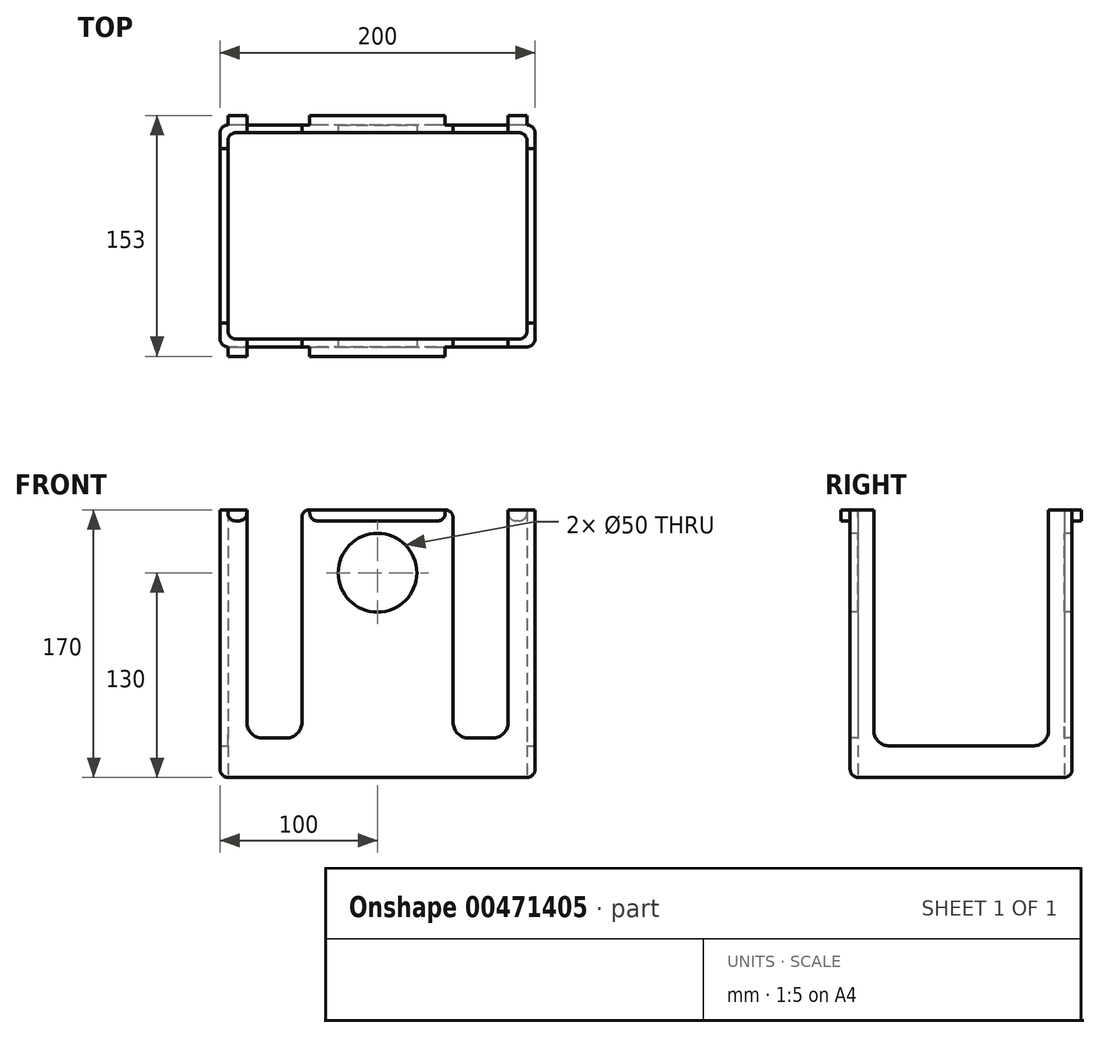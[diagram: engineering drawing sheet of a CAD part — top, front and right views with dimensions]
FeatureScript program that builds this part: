
annotation { "Feature Type Name" : "Feature", "Feature Type Description" : "" }
export const myFeature = defineFeature(function(context is Context, id is Id, definition is map)
    precondition{}
    {
        {
            var Q0;
            Q0=qCreatedBy(makeId("Top.planeOp"),FACE);
            var sketch = newSketch(context, id + "F0", { "sketchPlane" : qUnion([Q0])});
            skLineSegment(sketch, "E0.bottom", {"start": v(95, 70.5) * mm, "end": v(-95, 70.5) * mm});
            skLineSegment(sketch, "E0.top", {"start": v(95, -70.5) * mm, "end": v(-95, -70.5) * mm});
            skLineSegment(sketch, "E0.left", {"start": v(100, 65.5) * mm, "end": v(100, -65.5) * mm});
            skLineSegment(sketch, "E0.right", {"start": v(-100, 65.5) * mm, "end": v(-100, -65.5) * mm});
            skPoint(sketch, "E0.middle", {"position": v(0, 0) * mm});
            skPoint(sketch, "E1.visualSharp", {"position": v(-100, 70.5) * mm});
            skArc(sketch, "E1.filletArc", {"start": v(-95, 70.5) * mm, "mid": v(-98.54, 69.04) * mm, "end": v(-100, 65.5) * mm});
            skPoint(sketch, "E2.visualSharp", {"position": v(100, 70.5) * mm});
            skArc(sketch, "E2.filletArc", {"start": v(100, 65.5) * mm, "mid": v(98.54, 69.04) * mm, "end": v(95, 70.5) * mm});
            skPoint(sketch, "E3.visualSharp", {"position": v(100, -70.5) * mm});
            skArc(sketch, "E3.filletArc", {"start": v(95, -70.5) * mm, "mid": v(98.54, -69.04) * mm, "end": v(100, -65.5) * mm});
            skPoint(sketch, "E4.visualSharp", {"position": v(-100, -70.5) * mm});
            skArc(sketch, "E4.filletArc", {"start": v(-100, -65.5) * mm, "mid": v(-98.54, -69.04) * mm, "end": v(-95, -70.5) * mm});
            skLineSegment(sketch, "E5.bottom", {"start": v(90, 65.5) * mm, "end": v(-90, 65.5) * mm});
            skLineSegment(sketch, "E5.top", {"start": v(90, -65.5) * mm, "end": v(-90, -65.5) * mm});
            skLineSegment(sketch, "E5.left", {"start": v(95, 60.5) * mm, "end": v(95, -60.5) * mm});
            skLineSegment(sketch, "E5.right", {"start": v(-95, 60.5) * mm, "end": v(-95, -60.5) * mm});
            skArc(sketch, "E6.filletArc", {"start": v(-90, 65.5) * mm, "mid": v(-93.54, 64.04) * mm, "end": v(-95, 60.5) * mm});
            skArc(sketch, "E7.filletArc", {"start": v(95, 60.5) * mm, "mid": v(93.54, 64.04) * mm, "end": v(90, 65.5) * mm});
            skArc(sketch, "E8.filletArc", {"start": v(90, -65.5) * mm, "mid": v(93.54, -64.04) * mm, "end": v(95, -60.5) * mm});
            skArc(sketch, "E9.filletArc", {"start": v(-95, -60.5) * mm, "mid": v(-93.54, -64.04) * mm, "end": v(-90, -65.5) * mm});
            skSolve(sketch);
        }
        {
            var Q0;
            Q0 = qSketchRegion(id + "F0", true);
            extrude(context, id + "F1", {"entities" : qUnion([Q0]), "depth" : 170 * mm});
        }
        {
            var Q0;
            Q0=makeQuery(id+"F1.opExtrude","SWEPT_FACE",FACE,{"disambiguationData":[OSD([sQuery(id+"F0.wireOp",EDGE,"E0.top")])]});
            var sketch = newSketch(context, id + "F2", { "sketchPlane" : qUnion([Q0])});
            skCircle(sketch, "E10", {"center": v(0, 130) * mm, "radius": 25 * mm});
            skLineSegment(sketch, "E11.bottom", {"start": v(-83, 170) * mm, "end": v(-48, 170) * mm});
            skLineSegment(sketch, "E11.top", {"start": v(-73, 25) * mm, "end": v(-58, 25) * mm});
            skLineSegment(sketch, "E11.left", {"start": v(-83, 170) * mm, "end": v(-83, 35) * mm});
            skLineSegment(sketch, "E11.right", {"start": v(-48, 170) * mm, "end": v(-48, 35) * mm});
            skLineSegment(sketch, "E12.bottom", {"start": v(48, 170) * mm, "end": v(83, 170) * mm});
            skLineSegment(sketch, "E12.top", {"start": v(58, 25) * mm, "end": v(73, 25) * mm});
            skLineSegment(sketch, "E12.left", {"start": v(48, 170) * mm, "end": v(48, 35) * mm});
            skLineSegment(sketch, "E12.right", {"start": v(83, 170) * mm, "end": v(83, 35) * mm});
            skPoint(sketch, "E13.visualSharp", {"position": v(-83, 25) * mm});
            skArc(sketch, "E13.filletArc", {"start": v(-83, 35) * mm, "mid": v(-80.07, 27.93) * mm, "end": v(-73, 25) * mm});
            skPoint(sketch, "E14.visualSharp", {"position": v(-48, 25) * mm});
            skArc(sketch, "E14.filletArc", {"start": v(-58, 25) * mm, "mid": v(-50.93, 27.93) * mm, "end": v(-48, 35) * mm});
            skPoint(sketch, "E15.visualSharp", {"position": v(48, 25) * mm});
            skArc(sketch, "E15.filletArc", {"start": v(48, 35) * mm, "mid": v(50.93, 27.93) * mm, "end": v(58, 25) * mm});
            skPoint(sketch, "E16.visualSharp", {"position": v(83, 25) * mm});
            skArc(sketch, "E16.filletArc", {"start": v(73, 25) * mm, "mid": v(80.07, 27.93) * mm, "end": v(83, 35) * mm});
            skSolve(sketch);
        }
        {
            var Q0;
            Q0=makeQuery(id+"F2.imprint","IMPRINT",FACE,{"disambiguationData":[TD([[makeQuery(id+"F2.imprint","IMPRINT",EDGE,{"derivedFrom":sQuery(id+"F2.wireOp",EDGE,"E10")}),1.0]])]});
            var Q1;
            Q1=makeQuery(id+"F2.imprint","IMPRINT",FACE,{"disambiguationData":[TD([[makeQuery(id+"F2.imprint","IMPRINT",EDGE,{"derivedFrom":sQuery(id+"F2.wireOp",EDGE,"E11.bottom")}),1.0]])]});
            var Q2;
            Q2=makeQuery(id+"F2.imprint","IMPRINT",FACE,{"disambiguationData":[TD([[makeQuery(id+"F2.imprint","IMPRINT",EDGE,{"derivedFrom":sQuery(id+"F2.wireOp",EDGE,"E12.bottom")}),1.0]])]});
            extrude(context, id + "F3", {"entities" : qUnion([Q0, Q1, Q2]), "operationType" : NewBodyOperationType.REMOVE, "oppositeDirection" : true, "depth" : 250 * mm});
        }
        {
            var Q0;
            Q0=makeQuery(id+"F1.opExtrude","SWEPT_FACE",FACE,{"disambiguationData":[OSD([sQuery(id+"F0.wireOp",EDGE,"E0.left")])]});
            var sketch = newSketch(context, id + "F4", { "sketchPlane" : qUnion([Q0])});
            skLineSegment(sketch, "E17.bottom", {"start": v(-55.5, 170) * mm, "end": v(55.5, 170) * mm});
            skLineSegment(sketch, "E17.top", {"start": v(-45.5, 20) * mm, "end": v(45.5, 20) * mm});
            skLineSegment(sketch, "E17.left", {"start": v(-55.5, 170) * mm, "end": v(-55.5, 30) * mm});
            skLineSegment(sketch, "E17.right", {"start": v(55.5, 170) * mm, "end": v(55.5, 30) * mm});
            skPoint(sketch, "E18.visualSharp", {"position": v(-55.5, 170) * mm});
            skLineSegment(sketch, "E18.filletArc", {"start": v(-55.5, 170) * mm, "end": v(-55.5, 170) * mm});
            skPoint(sketch, "E19.visualSharp", {"position": v(55.5, 170) * mm});
            skLineSegment(sketch, "E19.filletArc", {"start": v(55.5, 170) * mm, "end": v(55.5, 170) * mm});
            skPoint(sketch, "E20.visualSharp", {"position": v(-55.5, 20) * mm});
            skArc(sketch, "E20.filletArc", {"start": v(-55.5, 30) * mm, "mid": v(-52.57, 22.93) * mm, "end": v(-45.5, 20) * mm});
            skPoint(sketch, "E21.visualSharp", {"position": v(55.5, 20) * mm});
            skArc(sketch, "E21.filletArc", {"start": v(45.5, 20) * mm, "mid": v(52.57, 22.93) * mm, "end": v(55.5, 30) * mm});
            skSolve(sketch);
        }
        {
            var Q0;
            Q0=makeQuery(id+"F4.imprint","IMPRINT",FACE,{"disambiguationData":[TD([[makeQuery(id+"F4.imprint","IMPRINT",EDGE,{"derivedFrom":sQuery(id+"F4.wireOp",EDGE,"E17.bottom")}),1.0]])]});
            extrude(context, id + "F5", {"entities" : qUnion([Q0]), "operationType" : NewBodyOperationType.REMOVE, "oppositeDirection" : true, "depth" : 210 * mm});
        }
        {
            var Q0;
            {var subQ1=sQuery(id+"F0.wireOp",EDGE,"E0.top");var subQ2=sQuery(id+"F2.wireOp",EDGE,"E11.right");Q0=makeQuery(id+"F3.boolean.opBoolean","COPY",EDGE,{"disambiguationData":[TD([makeQuery(id+"F1.opExtrude","SWEPT_FACE",FACE,{"disambiguationData":[OSD([subQ1])]})])],"derivedFrom":makeQuery(id+"F3.opExtrude","SWEPT_EDGE",EDGE,{"disambiguationData":[OSD([subQ1,sQuery(id+"F2.wireOp",EDGE,"E11.bottom"),subQ2])]})});}
            var Q1;
            {var subQ1=sQuery(id+"F0.wireOp",EDGE,"E0.top");var subQ2=sQuery(id+"F2.wireOp",EDGE,"E12.left");Q1=makeQuery(id+"F3.boolean.opBoolean","COPY",EDGE,{"disambiguationData":[TD([makeQuery(id+"F1.opExtrude","SWEPT_FACE",FACE,{"disambiguationData":[OSD([subQ1])]})])],"derivedFrom":makeQuery(id+"F3.opExtrude","SWEPT_EDGE",EDGE,{"disambiguationData":[OSD([subQ1,sQuery(id+"F2.wireOp",EDGE,"E12.bottom"),subQ2])]})});}
            var Q2;
            {var subQ0=sQuery(id+"F0.wireOp",EDGE,"E0.bottom");var subQ2=sQuery(id+"F0.wireOp",EDGE,"E0.top");var subQ3=sQuery(id+"F2.wireOp",EDGE,"E12.left");Q2=makeQuery(id+"F3.boolean.opBoolean","COPY",EDGE,{"disambiguationData":[TD([makeQuery(id+"F1.opExtrude","SWEPT_FACE",FACE,{"disambiguationData":[OSD([subQ0])]})])],"derivedFrom":makeQuery(id+"F3.opExtrude","SWEPT_EDGE",EDGE,{"disambiguationData":[OSD([subQ2,sQuery(id+"F2.wireOp",EDGE,"E12.bottom"),subQ3])]})});}
            var Q3;
            {var subQ0=sQuery(id+"F0.wireOp",EDGE,"E0.bottom");var subQ2=sQuery(id+"F0.wireOp",EDGE,"E0.top");var subQ3=sQuery(id+"F2.wireOp",EDGE,"E11.right");Q3=makeQuery(id+"F3.boolean.opBoolean","COPY",EDGE,{"disambiguationData":[TD([makeQuery(id+"F1.opExtrude","SWEPT_FACE",FACE,{"disambiguationData":[OSD([subQ0])]})])],"derivedFrom":makeQuery(id+"F3.opExtrude","SWEPT_EDGE",EDGE,{"disambiguationData":[OSD([subQ2,sQuery(id+"F2.wireOp",EDGE,"E11.bottom"),subQ3])]})});}
            fillet(context, id + "F6", {"entities" : qUnion([Q0, Q1, Q2, Q3]), "radius" : 5 * mm, "tangentPropagation" : true, "allowEdgeOverflow" : false});
        }
        {
            var Q0;
            Q0=makeQuery(id+"F1.opExtrude","SWEPT_FACE",FACE,{"disambiguationData":[OSD([sQuery(id+"F0.wireOp",EDGE,"E0.top")])]});
            var sketch = newSketch(context, id + "F7", { "sketchPlane" : qUnion([Q0])});
            skLineSegment(sketch, "E22.bottom", {"start": v(-43, 170) * mm, "end": v(43, 170) * mm});
            skLineSegment(sketch, "E22.top", {"start": v(-38.3, 163) * mm, "end": v(38.3, 163) * mm});
            skLineSegment(sketch, "E22.left", {"start": v(-43, 170) * mm, "end": v(-43, 167.7) * mm});
            skLineSegment(sketch, "E22.right", {"start": v(43, 170) * mm, "end": v(43, 167.7) * mm});
            skPoint(sketch, "E23.visualSharp", {"position": v(-43, 163) * mm});
            skArc(sketch, "E23.filletArc", {"start": v(-43, 167.7) * mm, "mid": v(-41.62, 164.38) * mm, "end": v(-38.3, 163) * mm});
            skPoint(sketch, "E24.visualSharp", {"position": v(43, 163) * mm});
            skArc(sketch, "E24.filletArc", {"start": v(38.3, 163) * mm, "mid": v(41.62, 164.38) * mm, "end": v(43, 167.7) * mm});
            skLineSegment(sketch, "E25.bottom", {"start": v(-95, 170) * mm, "end": v(-83, 170) * mm});
            skLineSegment(sketch, "E25.top", {"start": v(-90.3, 163) * mm, "end": v(-88, 163) * mm});
            skLineSegment(sketch, "E25.left", {"start": v(-95, 170) * mm, "end": v(-95, 167.7) * mm});
            skLineSegment(sketch, "E25.right", {"start": v(-83, 170) * mm, "end": v(-83, 168) * mm});
            skPoint(sketch, "E26.visualSharp", {"position": v(-95, 163) * mm});
            skArc(sketch, "E26.filletArc", {"start": v(-95, 167.7) * mm, "mid": v(-93.62, 164.38) * mm, "end": v(-90.3, 163) * mm});
            skPoint(sketch, "E27.visualSharp", {"position": v(-83, 163) * mm});
            skArc(sketch, "E27.filletArc", {"start": v(-88, 163) * mm, "mid": v(-84.46, 164.46) * mm, "end": v(-83, 168) * mm});
            skSolve(sketch);
        }
        {
            var Q0;
            Q0=makeQuery(id+"F7.imprint","IMPRINT",FACE,{"disambiguationData":[TD([[makeQuery(id+"F7.imprint","IMPRINT",EDGE,{"derivedFrom":sQuery(id+"F7.wireOp",EDGE,"E25.bottom")}),1.0]])]});
            var Q1;
            Q1=makeQuery(id+"F7.imprint","IMPRINT",FACE,{"disambiguationData":[TD([[makeQuery(id+"F7.imprint","IMPRINT",EDGE,{"derivedFrom":sQuery(id+"F7.wireOp",EDGE,"E22.bottom")}),1.0]])]});
            extrude(context, id + "F8", {"entities" : qUnion([Q0, Q1]), "operationType" : NewBodyOperationType.ADD, "depth" : 6 * mm});
        }
        {
            var Q0;
            Q0=makeQuery(id+"F1.opExtrude","CAP_EDGE",EDGE,{"disambiguationData":[OSD([sQuery(id+"F0.wireOp",EDGE,"E0.right")])],"isStart":true});
            fillet(context, id + "F9", {"entities" : qUnion([Q0]), "radius" : 5 * mm, "tangentPropagation" : true, "allowEdgeOverflow" : false});
        }
        {
            var Q0;
            Q0=makeQuery(id+"F1.opExtrude","SWEPT_FACE",FACE,{"disambiguationData":[OSD([sQuery(id+"F0.wireOp",EDGE,"E0.bottom")])]});
            var sketch = newSketch(context, id + "F10", { "sketchPlane" : qUnion([Q0])});
            skLineSegment(sketch, "E28.bottom", {"start": v(-43, 170) * mm, "end": v(43, 170) * mm});
            skLineSegment(sketch, "E28.top", {"start": v(-38, 163) * mm, "end": v(38, 163) * mm});
            skLineSegment(sketch, "E28.left", {"start": v(-43, 170) * mm, "end": v(-43, 168) * mm});
            skLineSegment(sketch, "E28.right", {"start": v(43, 170) * mm, "end": v(43, 168) * mm});
            skPoint(sketch, "E29.visualSharp", {"position": v(-43, 163) * mm});
            skArc(sketch, "E29.filletArc", {"start": v(-43, 168) * mm, "mid": v(-41.54, 164.46) * mm, "end": v(-38, 163) * mm});
            skPoint(sketch, "E30.visualSharp", {"position": v(43, 163) * mm});
            skArc(sketch, "E30.filletArc", {"start": v(38, 163) * mm, "mid": v(41.54, 164.46) * mm, "end": v(43, 168) * mm});
            skLineSegment(sketch, "E31.bottom", {"start": v(83, 170) * mm, "end": v(95, 170) * mm});
            skLineSegment(sketch, "E31.top", {"start": v(88, 163) * mm, "end": v(90, 163) * mm});
            skLineSegment(sketch, "E31.left", {"start": v(83, 170) * mm, "end": v(83, 168) * mm});
            skLineSegment(sketch, "E31.right", {"start": v(95, 170) * mm, "end": v(95, 168) * mm});
            skPoint(sketch, "E32.visualSharp", {"position": v(83, 163) * mm});
            skArc(sketch, "E32.filletArc", {"start": v(83, 168) * mm, "mid": v(84.46, 164.46) * mm, "end": v(88, 163) * mm});
            skPoint(sketch, "E33.visualSharp", {"position": v(95, 163) * mm});
            skArc(sketch, "E33.filletArc", {"start": v(90, 163) * mm, "mid": v(93.54, 164.46) * mm, "end": v(95, 168) * mm});
            skLineSegment(sketch, "E34.bottom", {"start": v(-95, 170) * mm, "end": v(-83, 170) * mm});
            skLineSegment(sketch, "E34.top", {"start": v(-90, 163) * mm, "end": v(-88, 163) * mm});
            skLineSegment(sketch, "E34.left", {"start": v(-95, 170) * mm, "end": v(-95, 168) * mm});
            skLineSegment(sketch, "E34.right", {"start": v(-83, 170) * mm, "end": v(-83, 168) * mm});
            skPoint(sketch, "E35.visualSharp", {"position": v(-95, 163) * mm});
            skArc(sketch, "E35.filletArc", {"start": v(-95, 168) * mm, "mid": v(-93.54, 164.46) * mm, "end": v(-90, 163) * mm});
            skPoint(sketch, "E36.visualSharp", {"position": v(-83, 163) * mm});
            skArc(sketch, "E36.filletArc", {"start": v(-88, 163) * mm, "mid": v(-84.46, 164.46) * mm, "end": v(-83, 168) * mm});
            skSolve(sketch);
        }
        {
            var Q0;
            Q0=makeQuery(id+"F10.imprint","IMPRINT",FACE,{"disambiguationData":[TD([[makeQuery(id+"F10.imprint","IMPRINT",EDGE,{"derivedFrom":sQuery(id+"F10.wireOp",EDGE,"E34.bottom")}),-1.0]])]});
            var Q1;
            Q1=makeQuery(id+"F10.imprint","IMPRINT",FACE,{"disambiguationData":[TD([[makeQuery(id+"F10.imprint","IMPRINT",EDGE,{"derivedFrom":sQuery(id+"F10.wireOp",EDGE,"E28.bottom")}),-1.0]])]});
            var Q2;
            Q2=makeQuery(id+"F10.imprint","IMPRINT",FACE,{"disambiguationData":[TD([[makeQuery(id+"F10.imprint","IMPRINT",EDGE,{"derivedFrom":sQuery(id+"F10.wireOp",EDGE,"E31.bottom")}),-1.0]])]});
            extrude(context, id + "F11", {"entities" : qUnion([Q0, Q1, Q2]), "operationType" : NewBodyOperationType.ADD, "depth" : 6 * mm});
        }
    });
